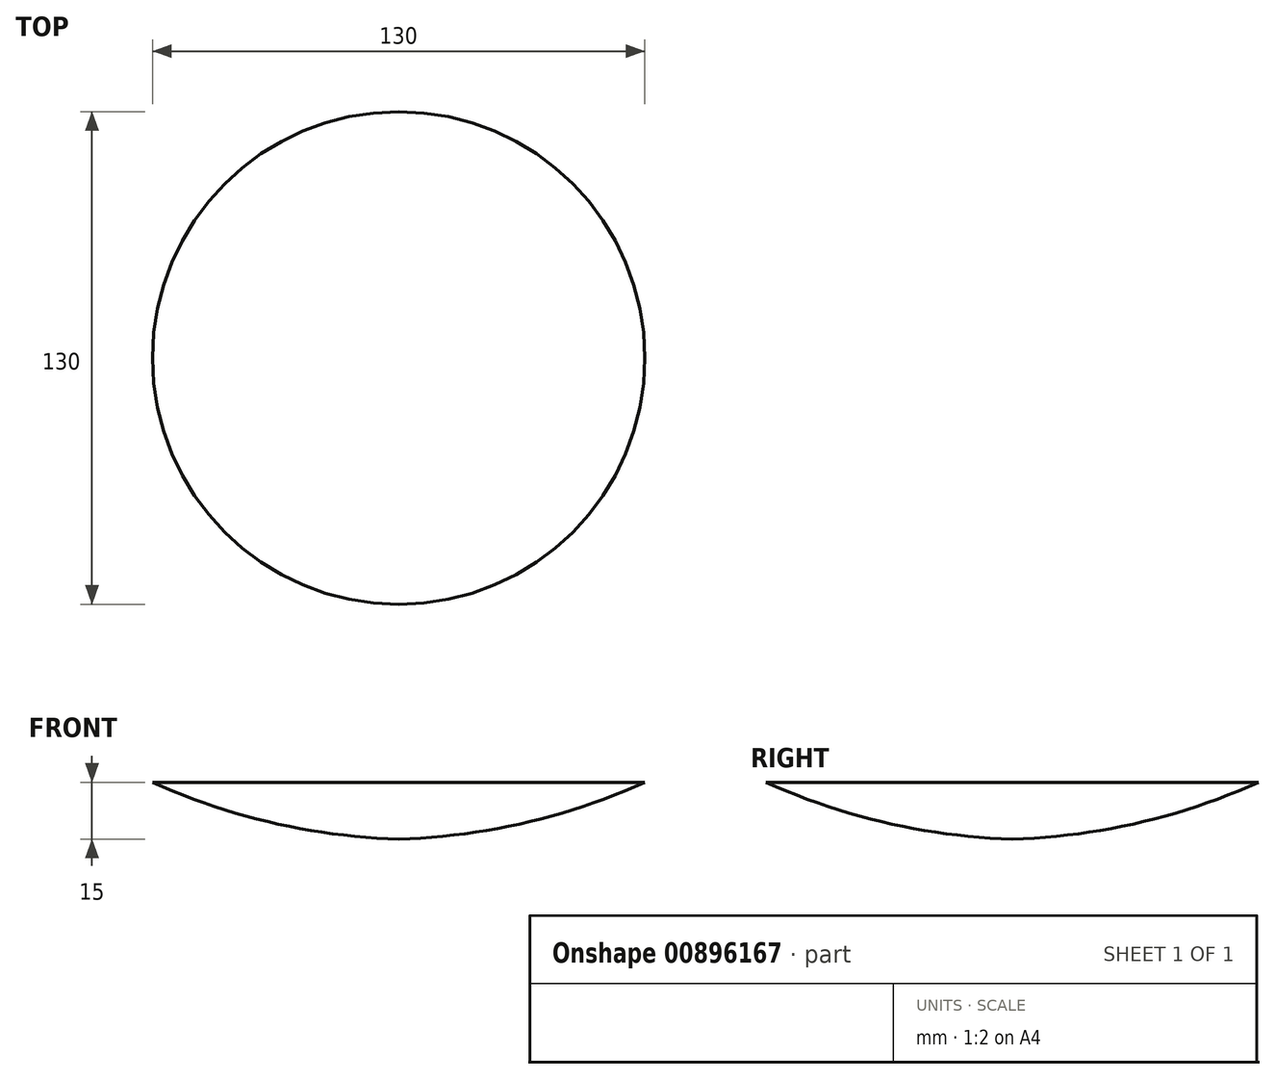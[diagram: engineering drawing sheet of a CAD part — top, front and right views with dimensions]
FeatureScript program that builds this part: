
annotation { "Feature Type Name" : "Feature", "Feature Type Description" : "" }
export const myFeature = defineFeature(function(context is Context, id is Id, definition is map)
    precondition{}
    {
        {
            var Q0;
            Q0=qCreatedBy(makeId("Front.planeOp"),FACE);
            var sketch = newSketch(context, id + "F0", { "sketchPlane" : qUnion([Q0])});
            skLineSegment(sketch, "E0", {"start": v(0, 0) * mm, "end": v(0, 43.97) * mm});
            skSolve(sketch);
        }
        {
            var Q0;
            Q0=qCreatedBy(makeId("Front.planeOp"),FACE);
            var sketch = newSketch(context, id + "F1", { "sketchPlane" : qUnion([Q0])});
            skLineSegment(sketch, "E1", {"start": v(0, 0) * mm, "end": v(65, 0) * mm});
            skLineSegment(sketch, "E2", {"start": v(0, 0) * mm, "end": v(0, -15) * mm});
            skArc(sketch, "E3", {"start": v(0, -15) * mm, "mid": v(33.24, -10.71) * mm, "end": v(65, 0) * mm});
            skSolve(sketch);
        }
        {
            var Q0;
            Q0=makeQuery(id+"F1.imprint","IMPRINT",FACE,{"disambiguationData":[TD([[makeQuery(id+"F1.imprint","IMPRINT",EDGE,{"derivedFrom":sQuery(id+"F1.wireOp",EDGE,"E1")}),-1.0]])]});
            var Q1;
            Q1=sQuery(id+"F0.wireOp",EDGE,"E0");
            revolve(context, id + "F2", {"surfaceOperationType" : NewSurfaceOperationType.NEW, "entities" : qUnion([Q0]), "axis" : qUnion([Q1]), "revolveType" : RevolveType.FULL});
        }
    });
